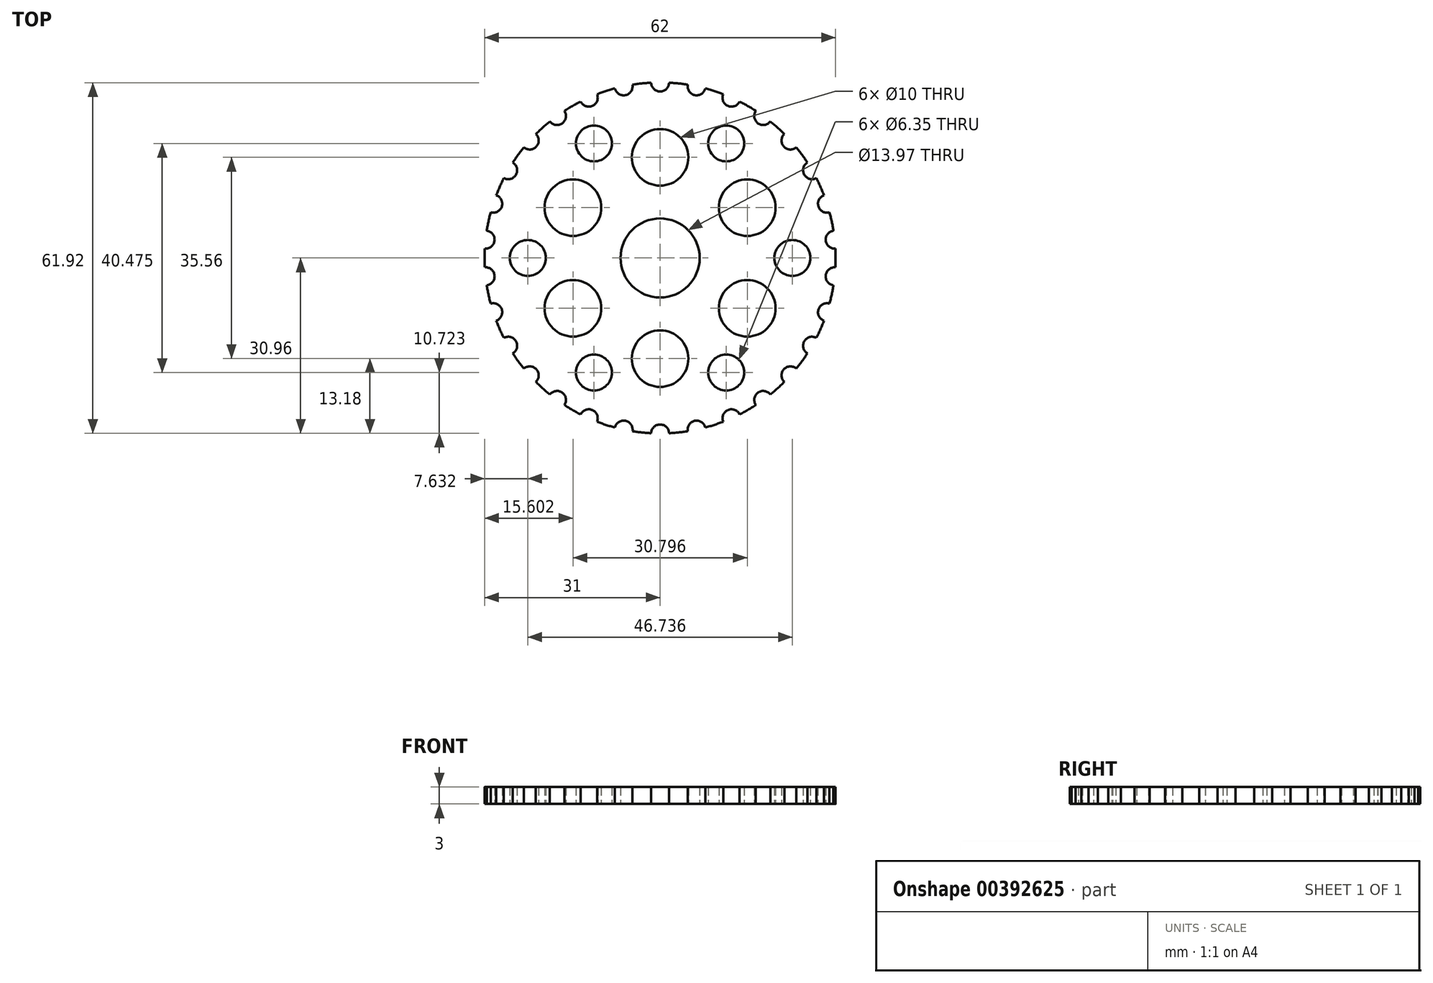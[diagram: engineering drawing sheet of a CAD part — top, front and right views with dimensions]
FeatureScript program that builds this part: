
annotation { "Feature Type Name" : "Feature", "Feature Type Description" : "" }
export const myFeature = defineFeature(function(context is Context, id is Id, definition is map)
    precondition{}
    {
        {
            var Q0;
            Q0=qCreatedBy(makeId("Top.planeOp"),FACE);
            var sketch = newSketch(context, id + "F0", { "sketchPlane" : qUnion([Q0])});
            skCircle(sketch, "E0", {"center": v(0, 0) * mm, "radius": 31 * mm});
            skCircle(sketch, "E1", {"center": v(0, 0) * mm, "radius": 6.99 * mm});
            skCircle(sketch, "E2", {"center": v(0, 17.78) * mm, "radius": 5 * mm});
            skLineSegment(sketch, "E3", {"start": v(0, 0) * mm, "end": v(0, 17.78) * mm});
            skCircle(sketch, "E4.1.0", {"center": v(-15.4, 8.9) * mm, "radius": 5 * mm});
            skCircle(sketch, "E4.2.0", {"center": v(-15.4, -8.89) * mm, "radius": 5 * mm});
            skCircle(sketch, "E4.3.0", {"center": v(0, -17.78) * mm, "radius": 5 * mm});
            skCircle(sketch, "E4.4.0", {"center": v(15.4, -8.9) * mm, "radius": 5 * mm});
            skCircle(sketch, "E4.5.0", {"center": v(15.4, 8.9) * mm, "radius": 5 * mm});
            skCircle(sketch, "E5", {"center": v(0, 31) * mm, "radius": 1.59 * mm});
            skCircle(sketch, "E6.1.0", {"center": v(-6.45, 30.32) * mm, "radius": 1.59 * mm});
            skCircle(sketch, "E6.2.0", {"center": v(-12.6, 28.32) * mm, "radius": 1.59 * mm});
            skCircle(sketch, "E6.3.0", {"center": v(-18.22, 25.08) * mm, "radius": 1.59 * mm});
            skCircle(sketch, "E6.4.0", {"center": v(-23.04, 20.74) * mm, "radius": 1.59 * mm});
            skCircle(sketch, "E6.5.0", {"center": v(-26.85, 15.5) * mm, "radius": 1.59 * mm});
            skCircle(sketch, "E6.6.0", {"center": v(-29.48, 9.58) * mm, "radius": 1.59 * mm});
            skCircle(sketch, "E6.7.0", {"center": v(-30.83, 3.24) * mm, "radius": 1.59 * mm});
            skCircle(sketch, "E6.8.0", {"center": v(-30.83, -3.24) * mm, "radius": 1.59 * mm});
            skCircle(sketch, "E6.9.0", {"center": v(-29.48, -9.58) * mm, "radius": 1.59 * mm});
            skCircle(sketch, "E6.10.0", {"center": v(-26.85, -15.5) * mm, "radius": 1.59 * mm});
            skCircle(sketch, "E6.11.0", {"center": v(-23.04, -20.74) * mm, "radius": 1.59 * mm});
            skCircle(sketch, "E6.12.0", {"center": v(-18.22, -25.08) * mm, "radius": 1.59 * mm});
            skCircle(sketch, "E6.13.0", {"center": v(-12.6, -28.32) * mm, "radius": 1.59 * mm});
            skCircle(sketch, "E6.14.0", {"center": v(-6.45, -30.32) * mm, "radius": 1.59 * mm});
            skCircle(sketch, "E6.15.0", {"center": v(0, -31) * mm, "radius": 1.59 * mm});
            skCircle(sketch, "E6.16.0", {"center": v(6.45, -30.32) * mm, "radius": 1.59 * mm});
            skCircle(sketch, "E6.17.0", {"center": v(12.6, -28.32) * mm, "radius": 1.59 * mm});
            skCircle(sketch, "E6.18.0", {"center": v(18.22, -25.08) * mm, "radius": 1.59 * mm});
            skCircle(sketch, "E6.19.0", {"center": v(23.04, -20.74) * mm, "radius": 1.59 * mm});
            skCircle(sketch, "E6.20.0", {"center": v(26.85, -15.5) * mm, "radius": 1.59 * mm});
            skCircle(sketch, "E6.21.0", {"center": v(29.48, -9.58) * mm, "radius": 1.59 * mm});
            skCircle(sketch, "E6.22.0", {"center": v(30.83, -3.24) * mm, "radius": 1.59 * mm});
            skCircle(sketch, "E6.23.0", {"center": v(30.83, 3.24) * mm, "radius": 1.59 * mm});
            skCircle(sketch, "E6.24.0", {"center": v(29.48, 9.58) * mm, "radius": 1.59 * mm});
            skCircle(sketch, "E6.25.0", {"center": v(26.85, 15.5) * mm, "radius": 1.59 * mm});
            skCircle(sketch, "E6.26.0", {"center": v(23.04, 20.74) * mm, "radius": 1.59 * mm});
            skCircle(sketch, "E6.27.0", {"center": v(18.22, 25.08) * mm, "radius": 1.59 * mm});
            skCircle(sketch, "E6.28.0", {"center": v(12.6, 28.32) * mm, "radius": 1.59 * mm});
            skCircle(sketch, "E6.29.0", {"center": v(6.45, 30.32) * mm, "radius": 1.59 * mm});
            skCircle(sketch, "E7", {"center": v(-11.68, 20.24) * mm, "radius": 3.18 * mm});
            skLineSegment(sketch, "E8", {"start": v(0, 0) * mm, "end": v(-11.68, 20.24) * mm});
            skLineSegment(sketch, "E9", {"start": v(0, 0) * mm, "end": v(-47.58, 0) * mm});
            skLineSegment(sketch, "E10", {"start": v(-47.58, 0) * mm, "end": v(0, 0) * mm});
            skCircle(sketch, "E11.1.0", {"center": v(-23.37, 0) * mm, "radius": 3.18 * mm});
            skCircle(sketch, "E11.2.0", {"center": v(-11.68, -20.24) * mm, "radius": 3.18 * mm});
            skCircle(sketch, "E11.3.0", {"center": v(11.68, -20.24) * mm, "radius": 3.18 * mm});
            skCircle(sketch, "E11.4.0", {"center": v(23.37, 0) * mm, "radius": 3.18 * mm});
            skCircle(sketch, "E11.5.0", {"center": v(11.68, 20.24) * mm, "radius": 3.18 * mm});
            skSolve(sketch);
        }
        {
            var Q0;
            Q0=makeQuery(id+"F0.imprint","IMPRINT",FACE,{"disambiguationData":[TD([[makeQuery(id+"F0.imprint","IMPRINT",EDGE,{"derivedFrom":sQuery(id+"F0.wireOp",EDGE,"E1")}),-1.0]])]});
            extrude(context, id + "F1", {"entities" : qUnion([Q0]), "depth" : 3 * mm});
        }
    });
